# Revit family: ElectricalFixture_WiringAccessories_Hager_Sollysta_PartMEuroAccomodationPlates
name_source: partatom
category: Electrical Fixtures
revit_build: Autodesk Revit 2015 (Build: 20160512_1515(x64)
units: mm (PartAtom-declared; Revit-internal decimal feet)

## types (3) — shared parameters
CE Approval = Yes
Colour = GreyPartM
Default Elevation = 1219.2 mm  [stored 4 ft]
Design Country = China
Expected Life = 25 years
Extrusion From Wall = 11.9 mm  [stored 0.039042 ft]
Finish = GreyPartM
Frequency = 50/60Hz
Gross Weight kg = 0.165
LED Indicator Switch = No
Manufacturer = Hager
Manufacturer Country = United Kingdom
Manufacturer Website = http://www.hager.co.uk
Material = Hager_GreyPartM
Overall Depth = 26.1 mm
Overall Height = 86 mm  [stored 0.282152 ft]
Packaging Recyclable = Yes
Product Family = WhiteMouldedEuroAccomodationPlates&Modules
Product Group = WiringAccessories
Product Literature = http://www.hager.co.uk
Product Range = Sollysta
Product URL = http://www.hager.co.uk
Reference Standard = BS 1363-2
Shape = Rectangular
Shipping Weight kg = 0.188
Supply Phase = 1
Switch = Yes
Type = ElectricalFixture
Voltage (Volts) = 230V/240V
zero-valued in all types: Overall Width

## per-type parameters (varying)
| type | 1Gang | 2Gang | 4Gang | Description | EAN Code | Features | Name | Overall Length | Product Model Number | Switch Width | SwitchHeight | Technical Description | Unique Reference |
| WMP1EUG | Yes | No | No | EuroStyleAccomodationPlate1ModuleGrey | 5015652261612 | EuroStyleAccomodationPlate1ModuleGrey | WhiteMouldedEuroAccomodationPlates&Modules_WMP1EUG | 86 mm  [stored 0.282152 ft] | WMP4EU | 100 mm  [stored 0.328084 ft] | 50 mm  [stored 0.164042 ft] | EuroStyleAccomodationPlate1ModuleGrey | WMP1EUG |
| WMP2EUG | No | Yes | No | EuroStyleAccomodationPlate2ModuleGrey | 5015652261605 | EuroStyleAccomodationPlate2ModuleGrey | WhiteMouldedEuroAccomodationPlates&Modules_WMP2EU | 86 mm  [stored 0.282152 ft] | WMP2EU | 50 mm  [stored 0.164042 ft] | 52.6 mm | EuroStyleAccomodationPlate2ModuleGrey | WMP2EU |
| WMP4EUG | No | Yes | Yes | EuroStyleAccomodationPlate4ModuleGrey | 5015652261612 | EuroStyleAccomodationPlate4ModuleGrey | WhiteMouldedEuroAccomodationPlates&Modules_WMP4EU | 146 mm  [stored 0.479003 ft] | WMP4EUG | 100 mm  [stored 0.328084 ft] | 50 mm  [stored 0.164042 ft] | EuroStyleAccomodationPlate4ModuleGrey | WMP4EUG |

note: [stored X ft] marks values corroborated as IEEE doubles in the binary element streams (Revit-internal decimal feet)

## geometry (parser evidence)
native form markers: Blend x4, Sweep x11
no freeform markers — native parametric forms only
